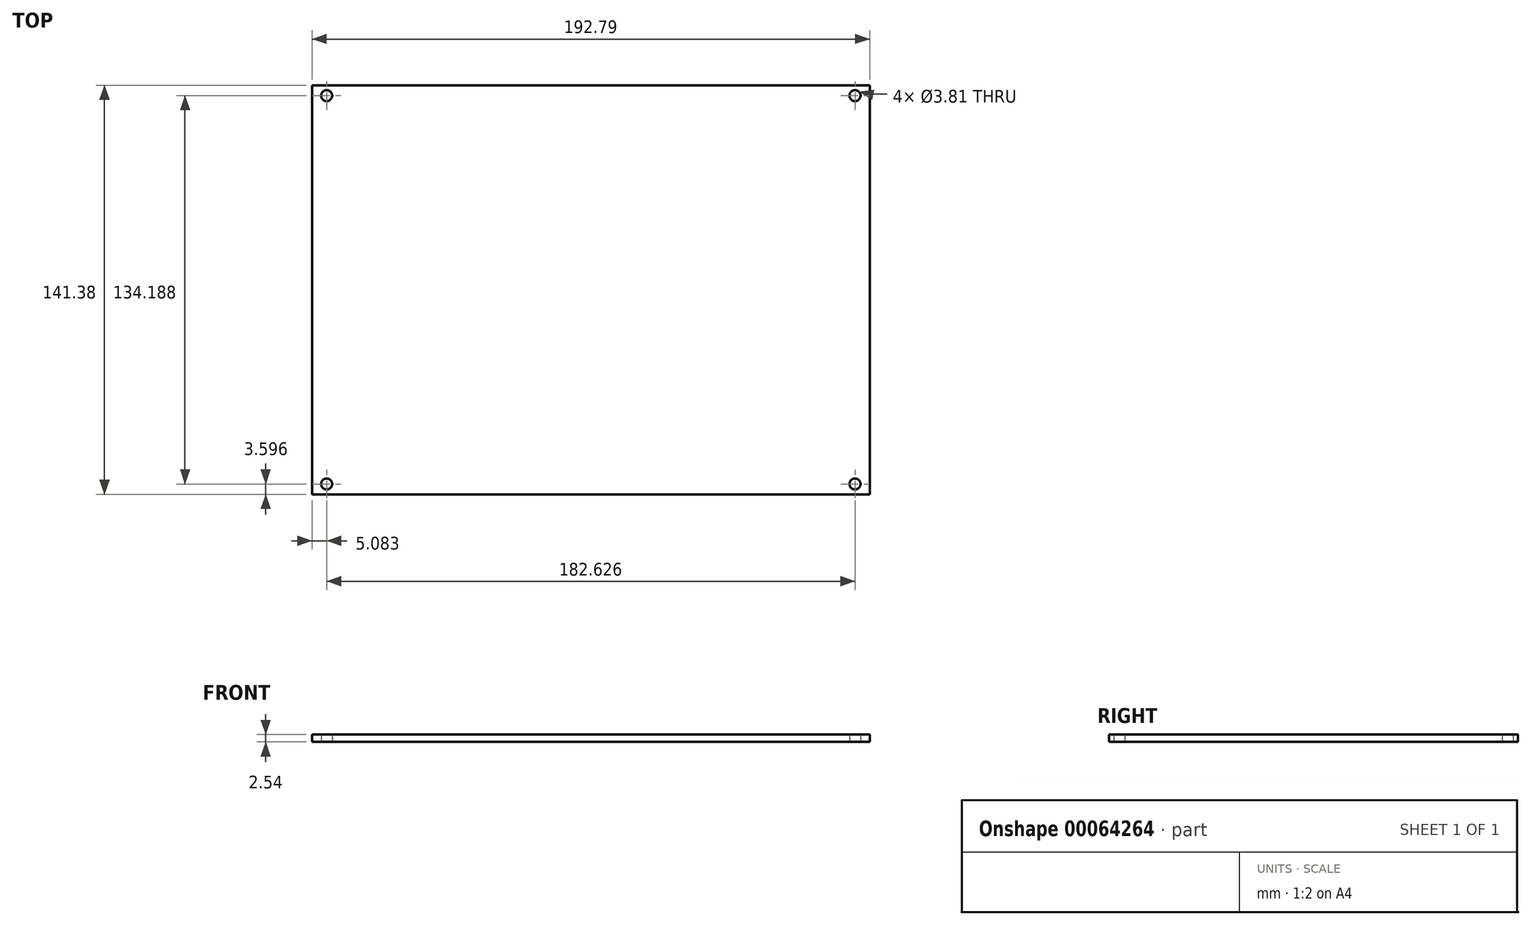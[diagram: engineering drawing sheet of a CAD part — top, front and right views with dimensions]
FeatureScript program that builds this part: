
annotation { "Feature Type Name" : "Feature", "Feature Type Description" : "" }
export const myFeature = defineFeature(function(context is Context, id is Id, definition is map)
    precondition{}
    {
        {
            var Q0;
            Q0=qCreatedBy(makeId("Top.planeOp"),FACE);
            var sketch = newSketch(context, id + "F0", { "sketchPlane" : qUnion([Q0])});
            skLineSegment(sketch, "E0.bottom", {"start": v(-98.88, 40.37) * mm, "end": v(3.23, 40.37) * mm});
            skLineSegment(sketch, "E0.top", {"start": v(-98.88, -13.48) * mm, "end": v(3.23, -13.48) * mm});
            skLineSegment(sketch, "E0.left", {"start": v(-98.88, 40.37) * mm, "end": v(-98.88, -13.48) * mm});
            skLineSegment(sketch, "E0.right", {"start": v(3.23, 40.37) * mm, "end": v(3.23, -13.48) * mm});
            skSolve(sketch);
        }
        {
            var Q0;
            Q0=qCreatedBy(makeId("Top.planeOp"),FACE);
            var sketch = newSketch(context, id + "F1", { "sketchPlane" : qUnion([Q0])});
            skLineSegment(sketch, "E1.bottom", {"start": v(-98.88, 40.37) * mm, "end": v(88.57, 40.37) * mm});
            skLineSegment(sketch, "E1.top", {"start": v(-98.88, -86.63) * mm, "end": v(88.57, -86.63) * mm});
            skLineSegment(sketch, "E1.left", {"start": v(-98.88, 40.37) * mm, "end": v(-98.88, -86.63) * mm});
            skLineSegment(sketch, "E1.right", {"start": v(88.57, 40.37) * mm, "end": v(88.57, -86.63) * mm});
            skSolve(sketch);
        }
        {
            var Q0;
            Q0=qCreatedBy(makeId("Top.planeOp"),FACE);
            var sketch = newSketch(context, id + "F2", { "sketchPlane" : qUnion([Q0])});
            skLineSegment(sketch, "E2.bottom", {"start": v(-101.17, 47.56) * mm, "end": v(91.62, 47.56) * mm});
            skLineSegment(sketch, "E2.top", {"start": v(-101.17, -93.82) * mm, "end": v(91.62, -93.82) * mm});
            skLineSegment(sketch, "E2.left", {"start": v(-101.17, 47.56) * mm, "end": v(-101.17, -93.82) * mm});
            skLineSegment(sketch, "E2.right", {"start": v(91.62, 47.56) * mm, "end": v(91.62, -93.82) * mm});
            skSolve(sketch);
        }
        {
            var Q0;
            Q0=qCreatedBy(makeId("Top.planeOp"),FACE);
            var sketch = newSketch(context, id + "F3", { "sketchPlane" : qUnion([Q0])});
            skCircle(sketch, "E3", {"center": v(-96.09, 43.96) * mm, "radius": 1.9 * mm});
            skCircle(sketch, "E4", {"center": v(86.54, 43.96) * mm, "radius": 1.9 * mm});
            skCircle(sketch, "E5", {"center": v(-96.09, -90.22) * mm, "radius": 1.9 * mm});
            skCircle(sketch, "E6", {"center": v(86.54, -90.22) * mm, "radius": 1.9 * mm});
            skSolve(sketch);
        }
        {
            var Q0;
            Q0=qSketchRegion(id+"F2",true);
            extrude(context, id + "F4", {"entities" : qUnion([Q0]), "depth" : 2.54 * mm, "offsetDistance" : 25.4 * mm});
        }
        {
            var Q0;
            Q0 = qSketchRegion(id + "F3", true);
            extrude(context, id + "F5", {"entities" : qUnion([Q0]), "operationType" : NewBodyOperationType.REMOVE, "depth" : 25.4 * mm, "offsetDistance" : 25.4 * mm});
        }
    });
